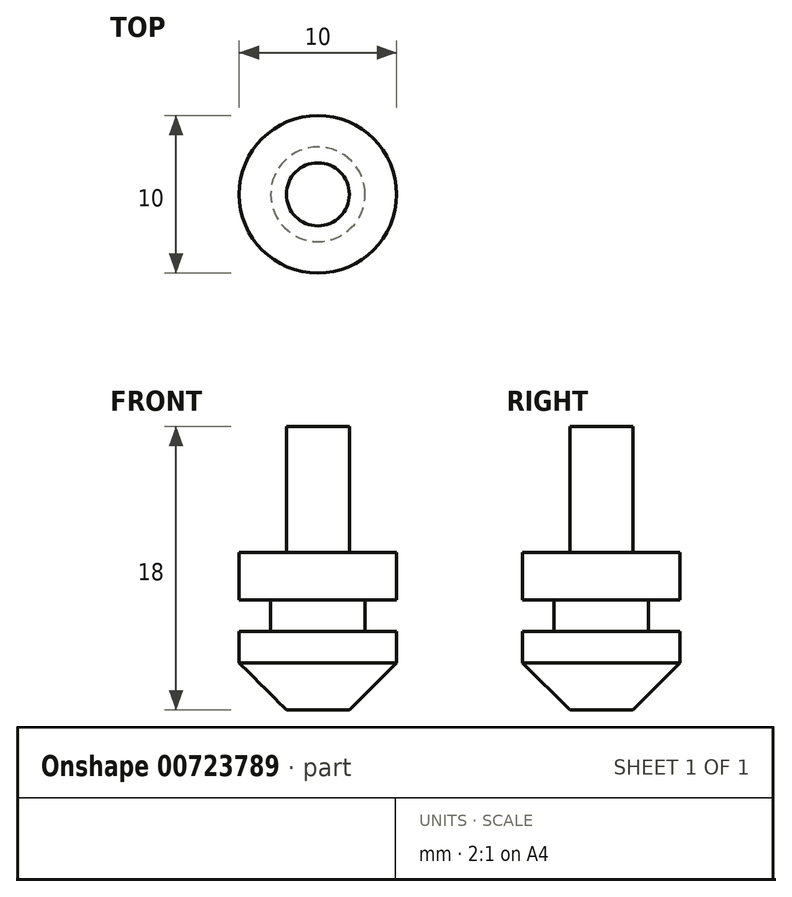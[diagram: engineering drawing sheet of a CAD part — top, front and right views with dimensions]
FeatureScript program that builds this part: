
annotation { "Feature Type Name" : "Feature", "Feature Type Description" : "" }
export const myFeature = defineFeature(function(context is Context, id is Id, definition is map)
    precondition{}
    {
        {
            var Q0;
            Q0=qCreatedBy(makeId("Front.planeOp"),FACE);
            var sketch = newSketch(context, id + "F0", { "sketchPlane" : qUnion([Q0])});
            skLineSegment(sketch, "E0", {"start": v(0, 0) * mm, "end": v(-2, 0) * mm});
            skLineSegment(sketch, "E1", {"start": v(-2, 0) * mm, "end": v(-2, -8) * mm});
            skLineSegment(sketch, "E2", {"start": v(-2, -8) * mm, "end": v(-5, -8) * mm});
            skLineSegment(sketch, "E3", {"start": v(-5, -8) * mm, "end": v(-5, -11) * mm});
            skLineSegment(sketch, "E4", {"start": v(-2, -18) * mm, "end": v(0, -18) * mm});
            skLineSegment(sketch, "E5", {"start": v(0, -18) * mm, "end": v(0, 0) * mm});
            skLineSegment(sketch, "E6", {"start": v(-2, -18) * mm, "end": v(-5, -15) * mm});
            skLineSegment(sketch, "E7", {"start": v(-5, -11) * mm, "end": v(-3, -11) * mm});
            skLineSegment(sketch, "E8", {"start": v(-3, -11) * mm, "end": v(-3, -13) * mm});
            skLineSegment(sketch, "E9", {"start": v(-3, -13) * mm, "end": v(-5, -13) * mm});
            skLineSegment(sketch, "E10.trimOffspring", {"start": v(-5, -13) * mm, "end": v(-5, -15) * mm});
            skSolve(sketch);
        }
        {
            var Q0;
            Q0=makeQuery(id+"F0.imprint","IMPRINT",FACE,{"disambiguationData":[TD([[makeQuery(id+"F0.imprint","IMPRINT",EDGE,{"derivedFrom":sQuery(id+"F0.wireOp",EDGE,"E0")}),1.0]])]});
            var Q1;
            Q1=sQuery(id+"F0.wireOp",EDGE,"E5");
            revolve(context, id + "F1", {"surfaceOperationType" : NewSurfaceOperationType.NEW, "entities" : qUnion([Q0]), "axis" : qUnion([Q1]), "revolveType" : RevolveType.FULL});
        }
    });
